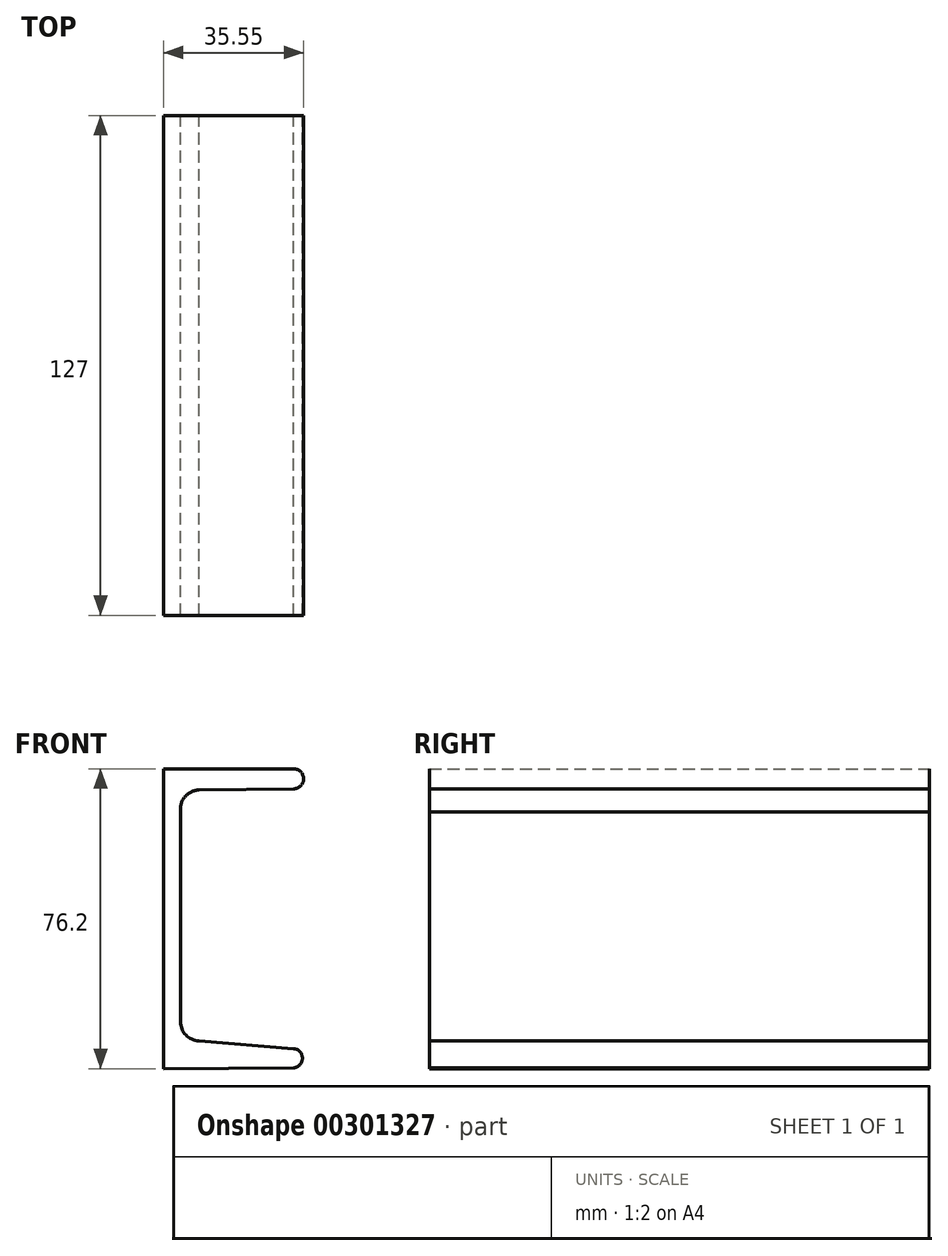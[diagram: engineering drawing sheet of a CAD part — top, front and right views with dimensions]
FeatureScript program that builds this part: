
annotation { "Feature Type Name" : "Feature", "Feature Type Description" : "" }
export const myFeature = defineFeature(function(context is Context, id is Id, definition is map)
    precondition{}
    {
        {
            var Q0;
            Q0=qCreatedBy(makeId("Front.planeOp"),FACE);
            var sketch = newSketch(context, id + "F0", { "sketchPlane" : qUnion([Q0])});
            skLineSegment(sketch, "E0", {"start": v(0, 0) * mm, "end": v(0, 76.2) * mm});
            skLineSegment(sketch, "E1", {"start": v(0, 76.2) * mm, "end": v(33.02, 76.2) * mm});
            skArc(sketch, "E2", {"start": v(33.01, 71.12) * mm, "mid": v(35.55, 73.66) * mm, "end": v(33.02, 76.2) * mm});
            skLineSegment(sketch, "E3", {"start": v(33.01, 71.12) * mm, "end": v(9.05, 70.8) * mm});
            skArc(sketch, "E4", {"start": v(9.05, 70.8) * mm, "mid": v(5.42, 69.09) * mm, "end": v(4.32, 65.22) * mm});
            skLineSegment(sketch, "E5", {"start": v(4.32, 65.22) * mm, "end": v(4.32, 11.91) * mm});
            skArc(sketch, "E6", {"start": v(4.32, 11.91) * mm, "mid": v(5.67, 8.56) * mm, "end": v(8.96, 7.07) * mm});
            skLineSegment(sketch, "E7", {"start": v(8.96, 7.07) * mm, "end": v(33.02, 5.09) * mm});
            skArc(sketch, "E8", {"start": v(33.02, 0.2) * mm, "mid": v(35.27, 2.65) * mm, "end": v(33.02, 5.09) * mm});
            skLineSegment(sketch, "E9", {"start": v(0, 0) * mm, "end": v(33.02, 0.2) * mm});
            skSolve(sketch);
        }
        {
            var Q0;
            Q0 = qSketchRegion(id + "F0", true);
            extrude(context, id + "F1", {"entities" : qUnion([Q0]), "endBound" : BoundingType.SYMMETRIC, "depth" : 127 * mm});
        }
    });
